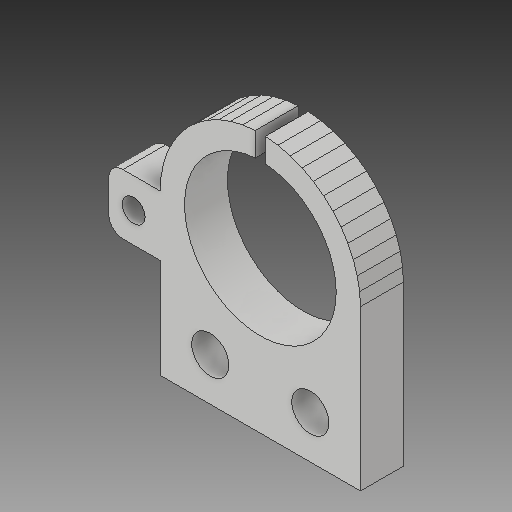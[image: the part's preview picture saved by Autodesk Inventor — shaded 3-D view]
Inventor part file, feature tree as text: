
AUTODESK INVENTOR PART (.ipt)
format: ipt  version: 2017 (Build 210142000, 142)  size: 205,312 bytes
history: native  units: mm
features: sketch x2, extrude x1, hole x1
ambient origin geometry x8: Origin, YZ Plane, XZ Plane, XY Plane, X Axis, Y Axis, Z Axis, Center Point
bodies: Solid1 (feature_tree)
feature tree (4):
  extrude  "Extrusion1"  [1 undecoded]
  hole  "Hole1"  [1 undecoded]
  sketch  "Sketch1"  dims[d0=6.0mm d1=0.0mm]
  sketch  "Sketch3"  dims[d2=21.2mm d3=6.0mm d4=4.0mm d5=2.0mm d6=90.0deg d7=8.0mm d8=20.594885mm]
note: 2 required parameter values undecoded (feature->parameter linkage not recoverable at this tier; creation-order binding heuristic only, values carry confidence <= 0.55)
